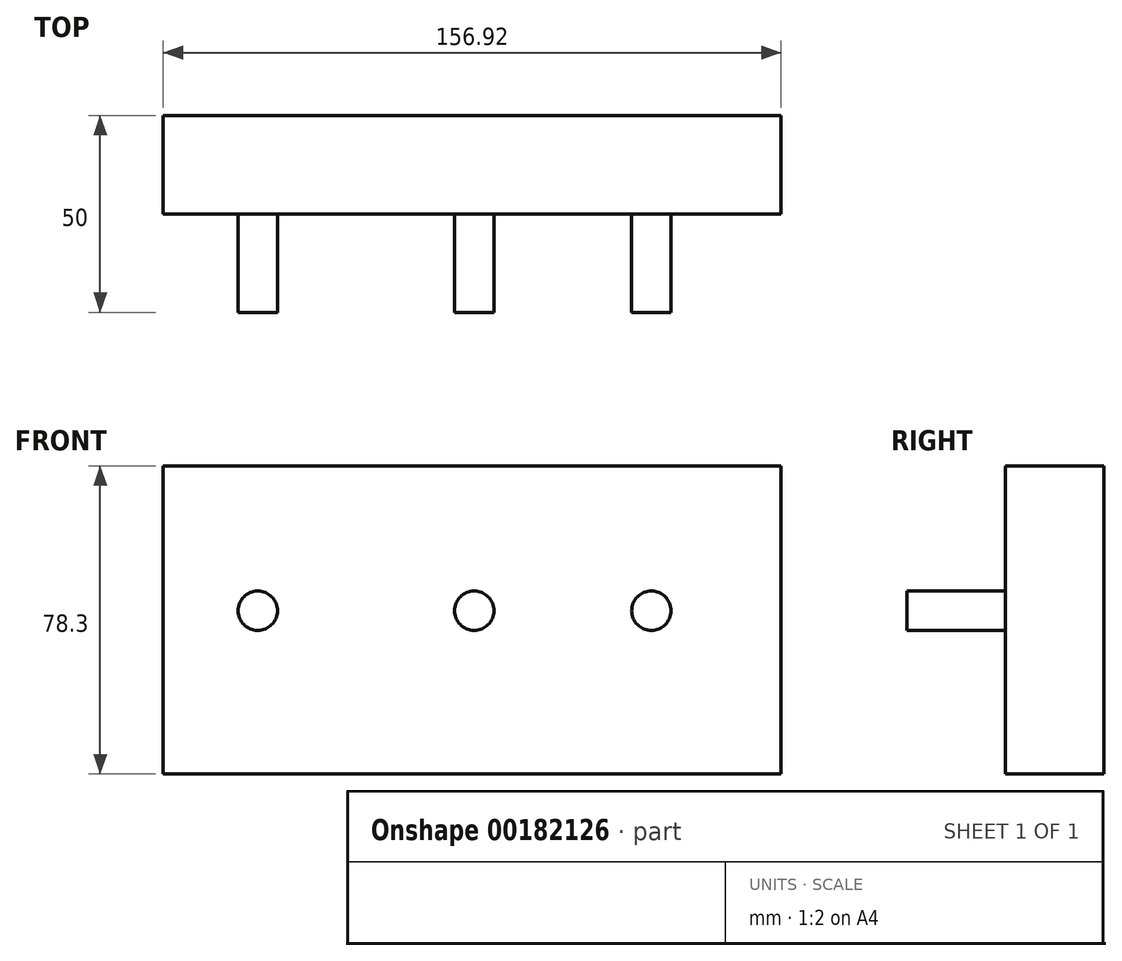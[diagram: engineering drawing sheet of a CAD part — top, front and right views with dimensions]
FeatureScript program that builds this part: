
annotation { "Feature Type Name" : "Feature", "Feature Type Description" : "" }
export const myFeature = defineFeature(function(context is Context, id is Id, definition is map)
    precondition{}
    {
        {
            var Q0;
            Q0=qCreatedBy(makeId("Front.planeOp"),FACE);
            var sketch = newSketch(context, id + "F0", { "sketchPlane" : qUnion([Q0])});
            skLineSegment(sketch, "E0.bottom", {"start": v(0, 0) * mm, "end": v(156.92, 0) * mm});
            skLineSegment(sketch, "E0.top", {"start": v(0, 78.3) * mm, "end": v(156.92, 78.3) * mm});
            skLineSegment(sketch, "E0.left", {"start": v(0, 0) * mm, "end": v(0, 78.3) * mm});
            skLineSegment(sketch, "E0.right", {"start": v(156.92, 0) * mm, "end": v(156.92, 78.3) * mm});
            skSolve(sketch);
        }
        {
            var Q0;
            Q0 = qSketchRegion(id + "F0", true);
            extrude(context, id + "F1", {"entities" : qUnion([Q0]), "depth" : 25 * mm});
        }
        {
            var Q0;
            Q0=makeQuery(id+"F1.opExtrude","CAP_FACE",FACE,{"disambiguationData":[OSD([sQuery(id+"F0.wireOp",EDGE,"E0.bottom"),sQuery(id+"F0.wireOp",EDGE,"E0.top"),sQuery(id+"F0.wireOp",EDGE,"E0.left"),sQuery(id+"F0.wireOp",EDGE,"E0.right")])],"isStart":false});
            var sketch = newSketch(context, id + "F2", { "sketchPlane" : qUnion([Q0])});
            skCircle(sketch, "E1", {"center": v(24, 41.48) * mm, "radius": 5 * mm});
            skCircle(sketch, "E2", {"center": v(79, 41.48) * mm, "radius": 5 * mm});
            skCircle(sketch, "E3", {"center": v(124, 41.48) * mm, "radius": 5 * mm});
            skSolve(sketch);
        }
        {
            var Q0;
            Q0 = qSketchRegion(id + "F2", true);
            extrude(context, id + "F3", {"entities" : qUnion([Q0]), "operationType" : NewBodyOperationType.ADD, "depth" : 25 * mm});
        }
    });
